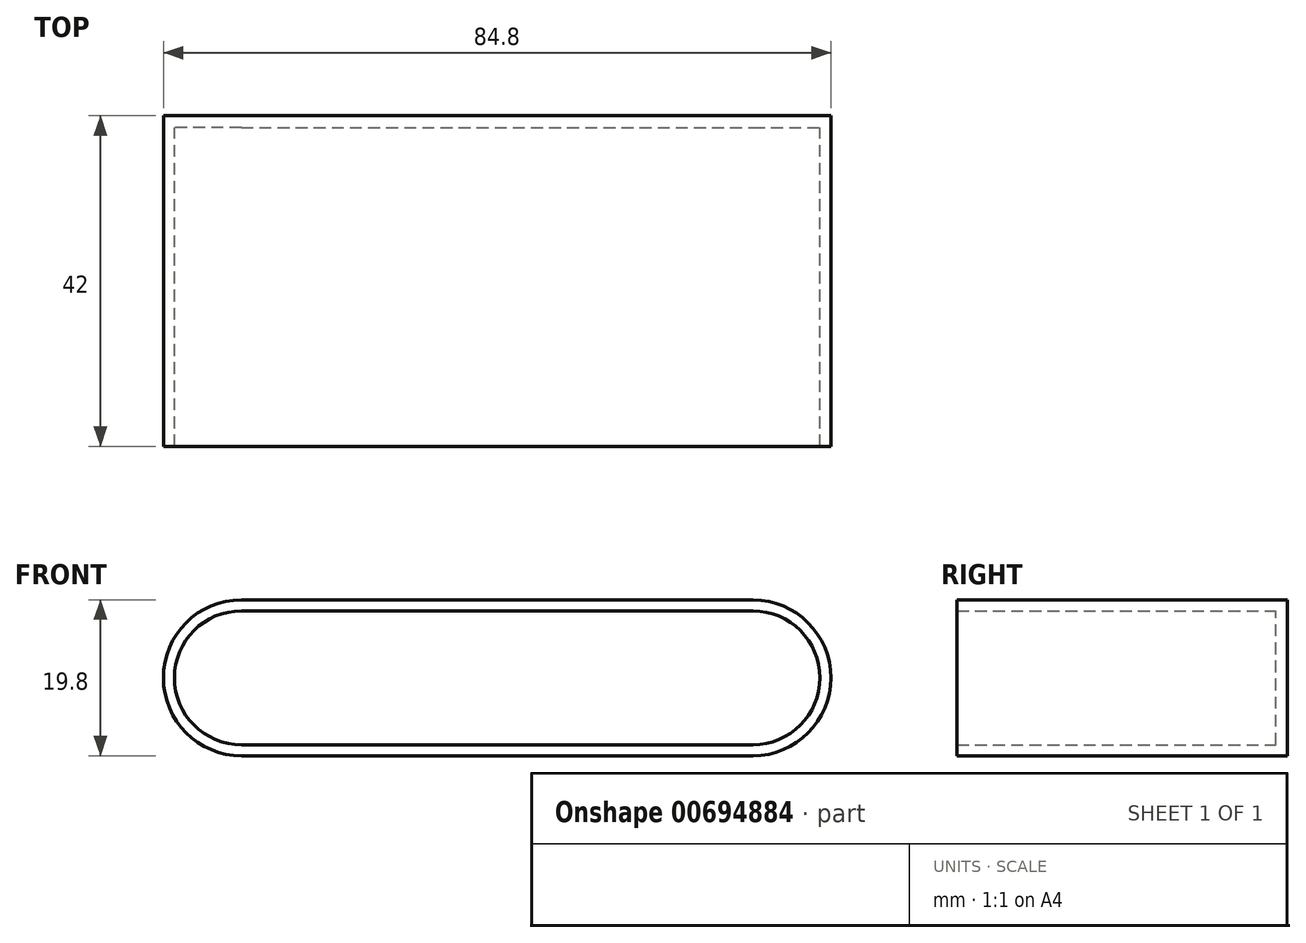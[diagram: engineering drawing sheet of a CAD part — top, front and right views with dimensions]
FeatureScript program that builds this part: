
annotation { "Feature Type Name" : "Feature", "Feature Type Description" : "" }
export const myFeature = defineFeature(function(context is Context, id is Id, definition is map)
    precondition{}
    {
        {
            var Q0;
            Q0=qCreatedBy(makeId("Front.planeOp"),FACE);
            var sketch = newSketch(context, id + "F0", { "sketchPlane" : qUnion([Q0])});
            skPoint(sketch, "E0.middle", {"position": v(0, 0) * mm});
            skLineSegment(sketch, "E1.bottom", {"start": v(-32.5, 12.5) * mm, "end": v(32.5, 12.5) * mm});
            skLineSegment(sketch, "E1.top", {"start": v(-32.5, -12.5) * mm, "end": v(32.5, -12.5) * mm});
            skLineSegment(sketch, "E2.bottom", {"start": v(-32.5, 10.5) * mm, "end": v(32.5, 10.5) * mm});
            skLineSegment(sketch, "E2.top", {"start": v(-32.5, -10.5) * mm, "end": v(32.5, -10.5) * mm});
            skArc(sketch, "E3", {"start": v(32.5, -12.5) * mm, "mid": v(45, 0) * mm, "end": v(32.5, 12.5) * mm});
            skArc(sketch, "E4", {"start": v(-32.5, 10.5) * mm, "mid": v(-43, 0) * mm, "end": v(-32.5, -10.5) * mm});
            skArc(sketch, "E5", {"start": v(-32.5, 12.5) * mm, "mid": v(-45, 0) * mm, "end": v(-32.5, -12.5) * mm});
            skArc(sketch, "E6", {"start": v(32.5, -10.5) * mm, "mid": v(43, 0) * mm, "end": v(32.5, 10.5) * mm});
            skLineSegment(sketch, "E7", {"start": v(-32.5, 10.5) * mm, "end": v(-32.5, 8.5) * mm});
            skLineSegment(sketch, "E8", {"start": v(-32.5, 8.5) * mm, "end": v(-32.5, 8) * mm});
            skLineSegment(sketch, "E9", {"start": v(-32.5, 8) * mm, "end": v(32.5, 8) * mm});
            skLineSegment(sketch, "E10", {"start": v(-32.5, 8.5) * mm, "end": v(32.5, 8.5) * mm});
            skLineSegment(sketch, "E11", {"start": v(32.5, -10.5) * mm, "end": v(32.5, -8.5) * mm});
            skLineSegment(sketch, "E12", {"start": v(32.5, -8.5) * mm, "end": v(32.5, -8) * mm});
            skLineSegment(sketch, "E13", {"start": v(32.5, -8) * mm, "end": v(-32.5, -8) * mm});
            skLineSegment(sketch, "E14", {"start": v(-32.5, -8.5) * mm, "end": v(32.5, -8.5) * mm});
            skArc(sketch, "E15", {"start": v(-32.5, 8) * mm, "mid": v(-40.5, 0) * mm, "end": v(-32.5, -8) * mm});
            skArc(sketch, "E16", {"start": v(-32.5, 8.5) * mm, "mid": v(-41, 0) * mm, "end": v(-32.5, -8.5) * mm});
            skArc(sketch, "E17", {"start": v(32.5, -8) * mm, "mid": v(40.5, 0) * mm, "end": v(32.5, 8) * mm});
            skArc(sketch, "E18", {"start": v(32.5, -8.5) * mm, "mid": v(41, 0) * mm, "end": v(32.5, 8.5) * mm});
            skLineSegment(sketch, "E19", {"start": v(-32.5, 10.5) * mm, "end": v(-32.5, 9.9) * mm});
            skLineSegment(sketch, "E20", {"start": v(32.5, 10.5) * mm, "end": v(32.5, 9.9) * mm});
            skLineSegment(sketch, "E21", {"start": v(32.5, 9.9) * mm, "end": v(-32.5, 9.9) * mm});
            skLineSegment(sketch, "E22", {"start": v(32.5, -10.5) * mm, "end": v(32.5, -9.9) * mm});
            skLineSegment(sketch, "E23", {"start": v(-32.5, -10.5) * mm, "end": v(-32.5, -9.9) * mm});
            skLineSegment(sketch, "E24", {"start": v(-32.5, -9.9) * mm, "end": v(32.5, -9.9) * mm});
            skArc(sketch, "E25", {"start": v(32.5, -9.9) * mm, "mid": v(42.4, 0) * mm, "end": v(32.5, 9.9) * mm});
            skArc(sketch, "E26", {"start": v(-32.5, 9.9) * mm, "mid": v(-42.4, 0) * mm, "end": v(-32.5, -9.9) * mm});
            skSolve(sketch);
        }
        {
            var Q0;
            Q0=makeQuery(id+"F0.imprint","IMPRINT",FACE,{"disambiguationData":[TD([[makeQuery(id+"F0.imprint","IMPRINT",EDGE,{"derivedFrom":sQuery(id+"F0.wireOp",EDGE,"E9")}),-1.0]])]});
            var Q1;
            Q1=makeQuery(id+"F0.imprint","IMPRINT",FACE,{"disambiguationData":[TD([[makeQuery(id+"F0.imprint","IMPRINT",EDGE,{"derivedFrom":sQuery(id+"F0.wireOp",EDGE,"E8")}),1.0]])]});
            var Q2;
            Q2=makeQuery(id+"F0.imprint","IMPRINT",FACE,{"disambiguationData":[TD([[makeQuery(id+"F0.imprint","IMPRINT",EDGE,{"derivedFrom":sQuery(id+"F0.wireOp",EDGE,"E8")}),-1.0]])]});
            extrude(context, id + "F1", {"entities" : qUnion([Q0, Q1, Q2]), "depth" : 1.5 * mm, "offsetDistance" : 25 * mm});
        }
        {
            var Q0;
            {var subQ1=sQuery(id+"F0.wireOp",EDGE,"E10");Q0=makeQuery(id+"F0.imprint","IMPRINT",FACE,{"disambiguationData":[TD([[makeQuery(id+"F0.imprint","IMPRINT",EDGE,{"derivedFrom":subQ1}),1.0]])]});}
            var Q1;
            {var subQ3=sQuery(id+"F0.wireOp",EDGE,"E14");Q1=makeQuery(id+"F0.imprint","IMPRINT",FACE,{"disambiguationData":[TD([[makeQuery(id+"F0.imprint","IMPRINT",EDGE,{"derivedFrom":subQ3}),-1.0]])]});}
            extrude(context, id + "F2", {"entities" : qUnion([Q0, Q1]), "operationType" : NewBodyOperationType.ADD, "depth" : 42 * mm, "offsetDistance" : 25 * mm});
        }
    });
